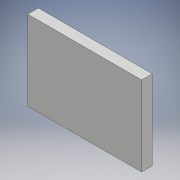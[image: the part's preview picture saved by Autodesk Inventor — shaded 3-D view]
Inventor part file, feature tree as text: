
AUTODESK INVENTOR PART (.ipt)
format: ipt  version: 2018.1 (Build 221171000, 171)  size: 92,672 bytes
history: native  units: mm
features: other x1, extrude x1, shell x1, sketch x1
ambient origin geometry x8: Origin, YZ Plane, XZ Plane, XY Plane, X Axis, Y Axis, Z Axis, Center Point
bodies: Body1 (feature_tree)
feature tree (4):
  other  "ソリッド1"
  extrude  "押し出し1"  Depth=75.0mm
  shell  "シェル1"  Thickness=107.0mm
  sketch  "スケッチ1"
